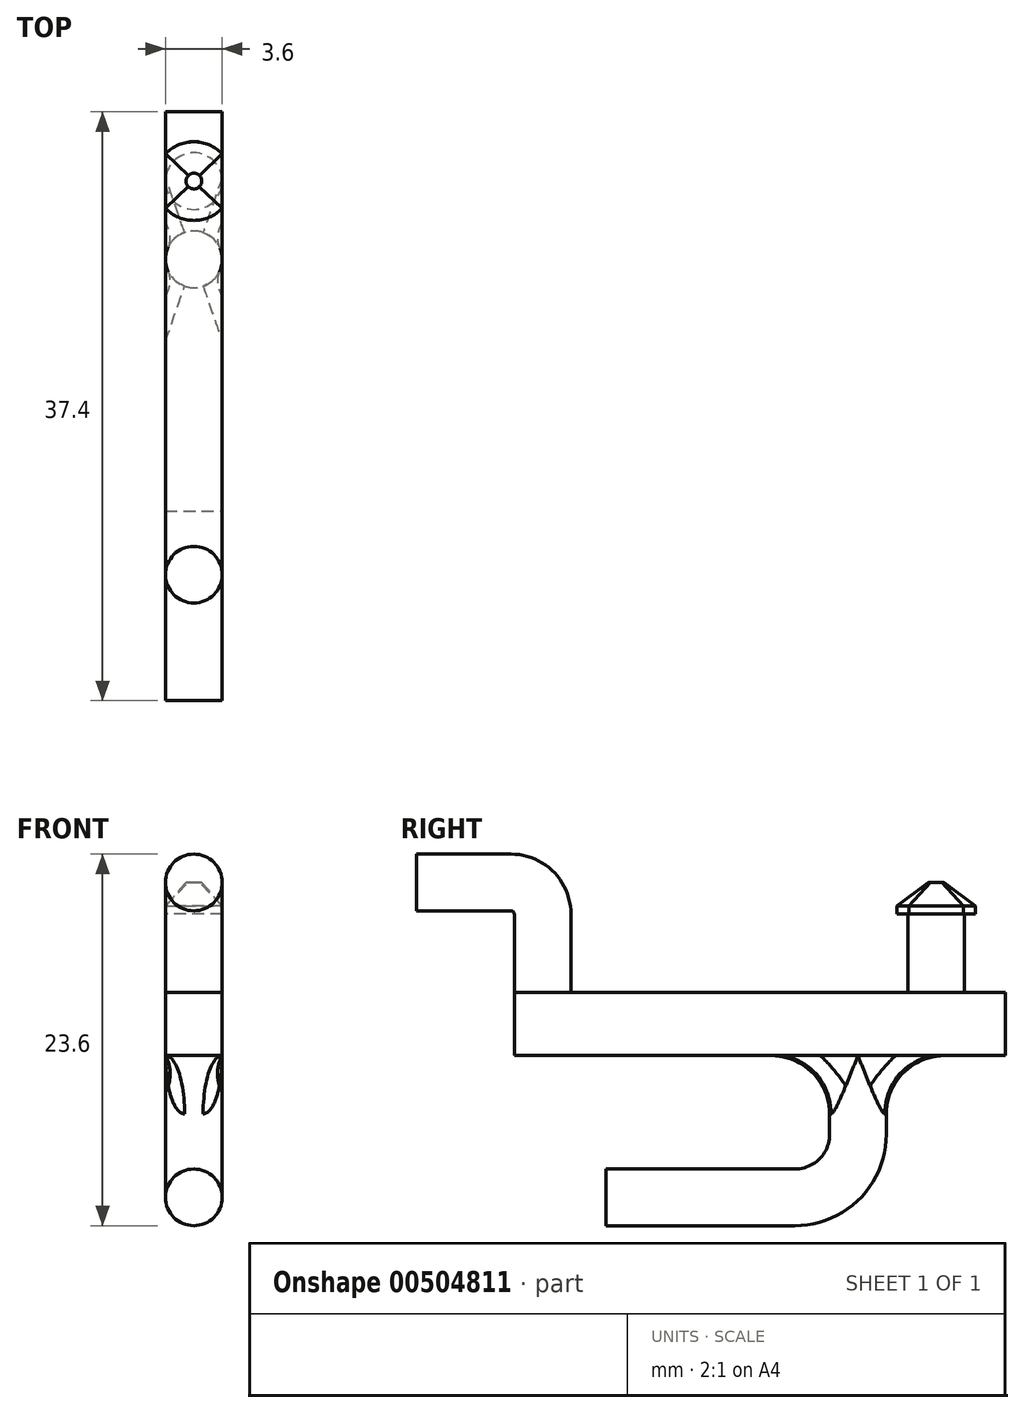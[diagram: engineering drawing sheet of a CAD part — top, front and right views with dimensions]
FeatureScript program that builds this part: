
annotation { "Feature Type Name" : "Feature", "Feature Type Description" : "" }
export const myFeature = defineFeature(function(context is Context, id is Id, definition is map)
    precondition{}
    {
        {
            var Q0;
            Q0=qCreatedBy(makeId("Top.planeOp"),FACE);
            var sketch = newSketch(context, id + "F0", { "sketchPlane" : qUnion([Q0])});
            skLineSegment(sketch, "E0.bottom", {"start": v(-1.8, 33.8) * mm, "end": v(1.8, 33.8) * mm});
            skLineSegment(sketch, "E0.top", {"start": v(-1.8, 0) * mm, "end": v(1.8, 0) * mm});
            skLineSegment(sketch, "E0.left", {"start": v(-1.8, 33.8) * mm, "end": v(-1.8, 0) * mm});
            skLineSegment(sketch, "E0.right", {"start": v(1.8, 33.8) * mm, "end": v(1.8, 0) * mm});
            skCircle(sketch, "E1", {"center": v(0, 29.4) * mm, "radius": 1.8 * mm});
            skPoint(sketch, "E1.centerSnap0", {"position": v(0, 33.8) * mm});
            skCircle(sketch, "E2", {"center": v(0, 4.4) * mm, "radius": 1.8 * mm});
            skPoint(sketch, "E2.centerSnap0", {"position": v(0, 0) * mm});
            skPoint(sketch, "E3", {"position": v(-9.75, 11.33) * mm});
            skSolve(sketch);
        }
        {
            var Q0;
            Q0=makeQuery(id+"F0.imprint","IMPRINT",FACE,{"disambiguationData":[TD([[makeQuery(id+"F0.imprint","IMPRINT",EDGE,{"derivedFrom":sQuery(id+"F0.wireOp",EDGE,"E1")}),1.0]])]});
            var Q1;
            Q1=makeQuery(id+"F0.imprint","IMPRINT",FACE,{"disambiguationData":[TD([[makeQuery(id+"F0.imprint","IMPRINT",EDGE,{"derivedFrom":sQuery(id+"F0.wireOp",EDGE,"E2")}),1.0]])]});
            extrude(context, id + "F1", {"entities" : qUnion([Q0, Q1]), "depth" : 5 * mm});
        }
        {
            var Q0;
            Q0=makeQuery(id+"F0.imprint","IMPRINT",FACE,{"disambiguationData":[TD([[makeQuery(id+"F0.imprint","IMPRINT",EDGE,{"derivedFrom":sQuery(id+"F0.wireOp",EDGE,"E1")}),1.0]])]});
            var Q1;
            Q1=makeQuery(id+"F0.imprint","IMPRINT",FACE,{"disambiguationData":[TD([[makeQuery(id+"F0.imprint","IMPRINT",EDGE,{"derivedFrom":sQuery(id+"F0.wireOp",EDGE,"E2")}),1.0]])]});
            var Q2;
            {var subQ0=sQuery(id+"F0.wireOp",EDGE,"E1");var subQ1=sQuery(id+"F0.wireOp",EDGE,"E0.left");var subQ2=makeQuery(id+"F0.imprint","INTERSECT",VERTEX,{"derivedFrom":[subQ1,subQ0]});Q2=makeQuery(id+"F0.imprint","IMPRINT",FACE,{"disambiguationData":[TD([[makeQuery(id+"F0.imprint","IMPRINT",EDGE,{"disambiguationData":[TD([[subQ2,-1.0]])],"derivedFrom":subQ1}),1.0]])]});}
            var Q3;
            {var subQ0=sQuery(id+"F0.wireOp",EDGE,"E0.bottom");Q3=makeQuery(id+"F0.imprint","IMPRINT",FACE,{"disambiguationData":[TD([[makeQuery(id+"F0.imprint","IMPRINT",EDGE,{"derivedFrom":subQ0}),-1.0]])]});}
            extrude(context, id + "F2", {"entities" : qUnion([Q0, Q1, Q2, Q3]), "oppositeDirection" : true, "depth" : 4 * mm});
        }
        {
            var Q0;
            Q0=makeQuery(id+"F1.opExtrude","CAP_FACE",FACE,{"disambiguationData":[OSD([sQuery(id+"F0.wireOp",EDGE,"E1")])],"isStart":false});
            var sketch = newSketch(context, id + "F3", { "sketchPlane" : qUnion([Q0])});
            skArc(sketch, "E4", {"start": v(-1.8, 27.67) * mm, "mid": v(0, 26.9) * mm, "end": v(1.8, 27.67) * mm});
            skLineSegment(sketch, "E5", {"start": v(-1.8, 27.67) * mm, "end": v(-1.8, 31.13) * mm});
            skLineSegment(sketch, "E6", {"start": v(1.8, 31.13) * mm, "end": v(1.8, 27.67) * mm});
            skArc(sketch, "E7.trimOffspring", {"start": v(1.8, 31.13) * mm, "mid": v(0, 31.9) * mm, "end": v(-1.8, 31.13) * mm});
            skSolve(sketch);
        }
        {
            var Q0;
            Q0=makeQuery(id+"F3.imprint","IMPRINT",FACE,{"disambiguationData":[TD([[makeQuery(id+"F3.imprint","IMPRINT",EDGE,{"derivedFrom":sQuery(id+"F3.wireOp",EDGE,"E4")}),1.0]])]});
            cPlane(context, id + "F4", {"entities" : qUnion([Q0]), "cplaneType" : CPlaneType.OFFSET, "offset" : 2 * mm, "width" : 150 * mm, "height" : 150 * mm});
        }
        {
            var Q0;
            Q0=qCreatedBy(id+"F4.planeOp",FACE);
            var sketch = newSketch(context, id + "F5", { "sketchPlane" : qUnion([Q0])});
            skCircle(sketch, "E8", {"center": v(0, 29.4) * mm, "radius": 0.5 * mm});
            skSolve(sketch);
        }
        {
            var Q0;
            Q0=makeQuery(id+"F3.imprint","IMPRINT",FACE,{"disambiguationData":[TD([[makeQuery(id+"F3.imprint","IMPRINT",EDGE,{"derivedFrom":makeQuery(id+"F1.opExtrude","CAP_EDGE",EDGE,{"disambiguationData":[OSD([sQuery(id+"F0.wireOp",EDGE,"E1")])],"isStart":false})}),1.0]])]});
            var Q1;
            Q1=makeQuery(id+"F3.imprint","IMPRINT",FACE,{"disambiguationData":[TD([[makeQuery(id+"F3.imprint","IMPRINT",EDGE,{"derivedFrom":sQuery(id+"F3.wireOp",EDGE,"E4")}),1.0]])]});
            var Q2;
            {var subQ0=sQuery(id+"F3.wireOp",EDGE,"E7.trimOffspring");Q2=makeQuery(id+"F3.imprint","IMPRINT",FACE,{"disambiguationData":[TD([[makeQuery(id+"F3.imprint","IMPRINT",EDGE,{"derivedFrom":subQ0}),1.0]])]});}
            extrude(context, id + "F6", {"entities" : qUnion([Q0, Q1, Q2]), "depth" : 0.5 * mm});
        }
        {
            var Q0;
            Q0=makeQuery(id+"F6.opExtrude","CAP_FACE",FACE,{"disambiguationData":[OSD([sQuery(id+"F3.wireOp",EDGE,"E4")])],"isStart":false});
            var Q1;
            Q1=makeQuery(id+"F5.imprint","IMPRINT",FACE,{"disambiguationData":[TD([[makeQuery(id+"F5.imprint","IMPRINT",EDGE,{"derivedFrom":sQuery(id+"F5.wireOp",EDGE,"E8")}),1.0]])]});
            loft(context, id + "F7", {"sheetProfilesArray" : [{ "sheetProfileEntities" : qUnion([Q0]) }, { "sheetProfileEntities" : qUnion([Q1]) }]});
        }
        {
            var Q0;
            Q0=makeQuery(id+"F1.opExtrude","CAP_FACE",FACE,{"disambiguationData":[OSD([sQuery(id+"F0.wireOp",EDGE,"E2")])],"isStart":false});
            var sketch = newSketch(context, id + "F8", { "sketchPlane" : qUnion([Q0])});
            skCircle(sketch, "E9", {"center": v(0, 4.4) * mm, "radius": 1.8 * mm});
            skSolve(sketch);
        }
        {
            var Q0;
            Q0=qCreatedBy(makeId("Right.planeOp"),FACE);
            var sketch = newSketch(context, id + "F9", { "sketchPlane" : qUnion([Q0])});
            skLineSegment(sketch, "E10", {"start": v(4.4, 5) * mm, "end": v(4.4, 5) * mm});
            skLineSegment(sketch, "E11", {"start": v(2.4, 7) * mm, "end": v(-3.6, 7) * mm});
            skPoint(sketch, "E12.visualSharp", {"position": v(4.4, 7) * mm});
            skArc(sketch, "E12.filletArc", {"start": v(4.4, 5) * mm, "mid": v(3.81, 6.41) * mm, "end": v(2.4, 7) * mm});
            skSolve(sketch);
        }
        {
            var Q0;
            Q0=makeQuery(id+"F8.imprint","IMPRINT",FACE,{"disambiguationData":[TD([[makeQuery(id+"F8.imprint","IMPRINT",EDGE,{"derivedFrom":sQuery(id+"F8.wireOp",EDGE,"E9")}),1.0]])]});
            var Q1;
            Q1=sQuery(id+"F9.wireOp",EDGE,"E10");
            var Q2;
            Q2=sQuery(id+"F9.wireOp",EDGE,"E12.filletArc");
            var Q3;
            Q3=sQuery(id+"F9.wireOp",EDGE,"E11");
            sweep(context, id + "F10", {"operationType" : NewBodyOperationType.ADD, "profiles" : qUnion([Q0]), "path" : qUnion([Q1, Q2, Q3])});
        }
        {
            var Q0;
            Q0=qCreatedBy(makeId("Right.planeOp"),FACE);
            var sketch = newSketch(context, id + "F11", { "sketchPlane" : qUnion([Q0])});
            skPoint(sketch, "E13", {"position": v(24.43, -4) * mm});
            skSolve(sketch);
        }
        {
            var Q0;
            Q0=makeQuery(id+"F2.opExtrude","CAP_FACE",FACE,{"disambiguationData":[OSD([sQuery(id+"F0.wireOp",EDGE,"E0.left"),sQuery(id+"F0.wireOp",EDGE,"E0.right"),sQuery(id+"F0.wireOp",EDGE,"E1"),sQuery(id+"F0.wireOp",EDGE,"E2")])],"isStart":false});
            var sketch = newSketch(context, id + "F12", { "sketchPlane" : qUnion([Q0])});
            skCircle(sketch, "E14", {"center": v(0, -24.43) * mm, "radius": 1.8 * mm});
            skSolve(sketch);
        }
        {
            var Q0;
            Q0 = qSketchRegion(id + "F12", true);
            extrude(context, id + "F13", {"entities" : qUnion([Q0]), "operationType" : NewBodyOperationType.ADD, "depth" : 5 * mm});
        }
        {
            var Q0;
            Q0=makeQuery(id+"F13.opExtrude","CAP_FACE",FACE,{"disambiguationData":[OSD([sQuery(id+"F12.wireOp",EDGE,"E14")])],"isStart":false});
            var sketch = newSketch(context, id + "F14", { "sketchPlane" : qUnion([Q0])});
            skPoint(sketch, "E15", {"position": v(0, -24.43) * mm});
            skSolve(sketch);
        }
        {
            var Q0;
            Q0=qCreatedBy(makeId("Right.planeOp"),FACE);
            var sketch = newSketch(context, id + "F15", { "sketchPlane" : qUnion([Q0])});
            skArc(sketch, "E16", {"start": v(20.43, -13) * mm, "mid": v(23.26, -11.83) * mm, "end": v(24.43, -9) * mm});
            skLineSegment(sketch, "E17", {"start": v(20.43, -13) * mm, "end": v(8.43, -13) * mm});
            skPoint(sketch, "E18.start.orphan", {"position": v(24.43, -9) * mm});
            skSolve(sketch);
        }
        {
            var Q0;
            Q0=makeQuery(id+"F14.imprint","IMPRINT",FACE,{"disambiguationData":[TD([[makeQuery(id+"F14.imprint","IMPRINT",EDGE,{"derivedFrom":makeQuery(id+"F13.opExtrude","CAP_EDGE",EDGE,{"disambiguationData":[OSD([sQuery(id+"F12.wireOp",EDGE,"E14")])],"isStart":false})}),1.0]])]});
            var Q1;
            Q1=sQuery(id+"F15.wireOp",EDGE,"E16");
            var Q2;
            Q2=sQuery(id+"F15.wireOp",EDGE,"E17");
            sweep(context, id + "F16", {"operationType" : NewBodyOperationType.ADD, "profiles" : qUnion([Q0]), "path" : qUnion([Q1, Q2])});
        }
        {
            var Q0;
            Q0=makeQuery(id+"F13.boolean.opBoolean","SPLIT",EDGE,{"disambiguationData":[OD(0.0)],"derivedFrom":makeQuery(id+"F13.opExtrude","CAP_EDGE",EDGE,{"disambiguationData":[OSD([sQuery(id+"F12.wireOp",EDGE,"E14")])],"isStart":true})});
            fillet(context, id + "F17", {"entities" : qUnion([Q0]), "radius" : 3.7 * mm, "tangentPropagation" : true, "allowEdgeOverflow" : false});
        }
    });
